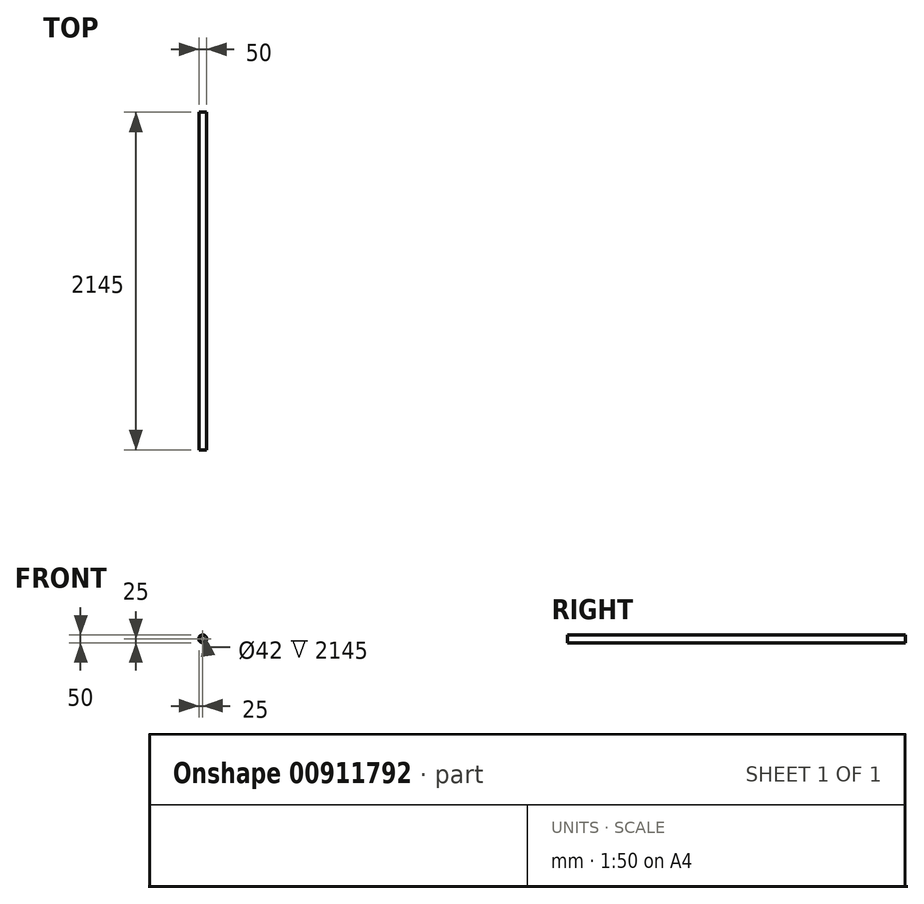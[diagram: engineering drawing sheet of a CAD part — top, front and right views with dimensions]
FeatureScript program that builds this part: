
annotation { "Feature Type Name" : "Feature", "Feature Type Description" : "" }
export const myFeature = defineFeature(function(context is Context, id is Id, definition is map)
    precondition{}
    {
        {
            var Q0;
            Q0=qCreatedBy(makeId("Front.planeOp"),FACE);
            var sketch = newSketch(context, id + "F0", { "sketchPlane" : qUnion([Q0])});
            skCircle(sketch, "E0", {"center": v(0, 0) * mm, "radius": 25 * mm});
            skCircle(sketch, "E1", {"center": v(0, 0) * mm, "radius": 21 * mm});
            skSolve(sketch);
        }
        {
            var Q0;
            Q0=makeQuery(id+"F0.imprint","IMPRINT",FACE,{"disambiguationData":[TD([[makeQuery(id+"F0.imprint","IMPRINT",EDGE,{"derivedFrom":sQuery(id+"F0.wireOp",EDGE,"E0")}),1.0]])]});
            extrude(context, id + "F1", {"entities" : qUnion([Q0]), "depth" : 2120 * mm, "offsetDistance" : 25 * mm, "hasSecondDirection" : true, "secondDirectionOppositeDirection" : true, "secondDirectionDepth" : 25 * mm});
        }
    });
